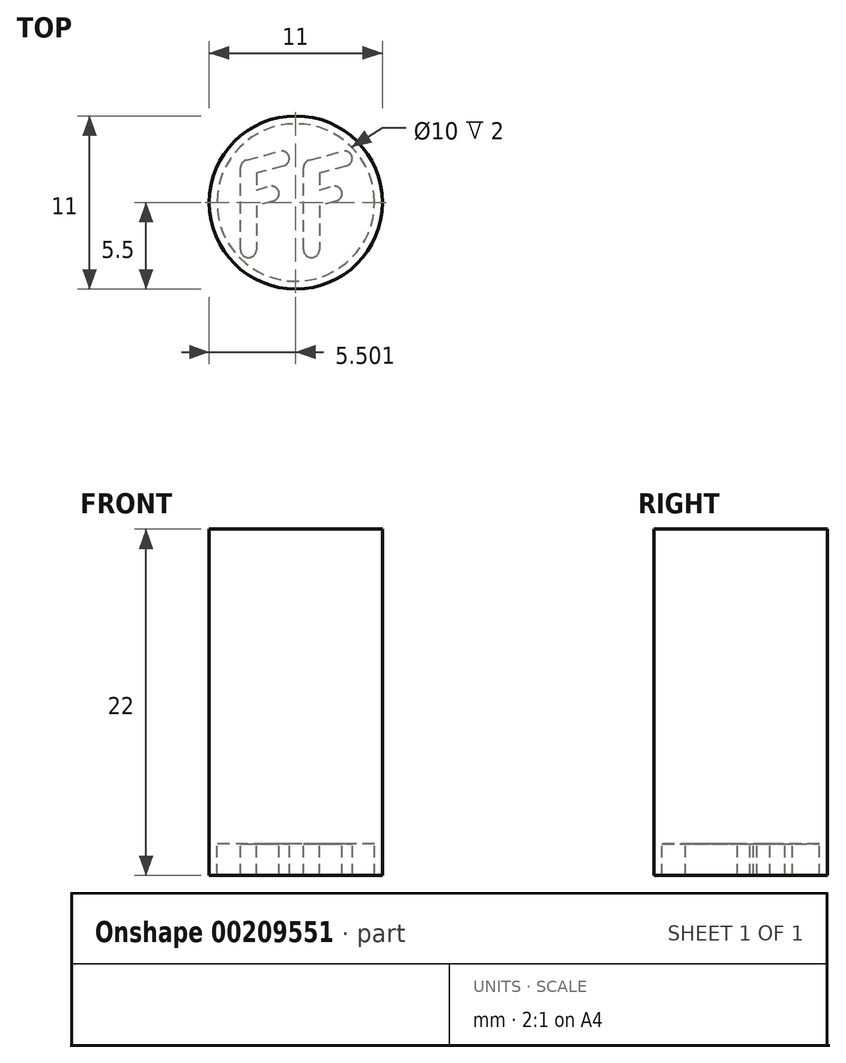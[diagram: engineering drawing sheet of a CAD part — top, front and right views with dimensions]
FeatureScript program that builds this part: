
annotation { "Feature Type Name" : "Feature", "Feature Type Description" : "" }
export const myFeature = defineFeature(function(context is Context, id is Id, definition is map)
    precondition{}
    {
        {
            var Q0;
            Q0=qCreatedBy(makeId("Top.planeOp"),FACE);
            var sketch = newSketch(context, id + "F0", { "sketchPlane" : qUnion([Q0])});
            skCircle(sketch, "E0", {"center": v(1.06, 0) * mm, "radius": 5 * mm});
            skCircle(sketch, "E1.0", {"center": v(1.06, 0) * mm, "radius": 5.5 * mm});
            skLineSegment(sketch, "E2", {"start": v(-2.44, -3.5) * mm, "end": v(-2.44, 2.6) * mm});
            skLineSegment(sketch, "E3", {"start": v(-2.44, 2.6) * mm, "end": v(0.65, 3.43) * mm});
            skLineSegment(sketch, "E4", {"start": v(0.65, 3.43) * mm, "end": v(0.65, 2.43) * mm});
            skLineSegment(sketch, "E5", {"start": v(0.65, 2.43) * mm, "end": v(-1.44, 1.87) * mm});
            skLineSegment(sketch, "E6", {"start": v(-1.44, 1.87) * mm, "end": v(-1.44, 0.8) * mm});
            skLineSegment(sketch, "E7", {"start": v(-1.44, 0.8) * mm, "end": v(0, 1.2) * mm});
            skLineSegment(sketch, "E8", {"start": v(0, 1.2) * mm, "end": v(0, 0.2) * mm});
            skLineSegment(sketch, "E9", {"start": v(0, 0.2) * mm, "end": v(-1.44, -0.2) * mm});
            skLineSegment(sketch, "E10", {"start": v(-1.44, -0.2) * mm, "end": v(-1.44, -3.5) * mm});
            skLineSegment(sketch, "E11", {"start": v(-1.44, -3.5) * mm, "end": v(-2.44, -3.5) * mm});
            skLineSegment(sketch, "E12.1.0.0", {"start": v(1.56, 2.6) * mm, "end": v(4.65, 3.43) * mm});
            skLineSegment(sketch, "E12.1.0.1", {"start": v(1.56, -3.5) * mm, "end": v(1.56, 2.6) * mm});
            skLineSegment(sketch, "E12.1.0.2", {"start": v(2.56, -3.5) * mm, "end": v(1.56, -3.5) * mm});
            skLineSegment(sketch, "E12.1.0.3", {"start": v(2.56, -0.2) * mm, "end": v(2.56, -3.5) * mm});
            skLineSegment(sketch, "E12.1.0.4", {"start": v(4, 0.2) * mm, "end": v(2.56, -0.2) * mm});
            skLineSegment(sketch, "E12.1.0.5", {"start": v(4, 1.2) * mm, "end": v(4, 0.2) * mm});
            skLineSegment(sketch, "E12.1.0.6", {"start": v(2.56, 0.8) * mm, "end": v(4, 1.2) * mm});
            skLineSegment(sketch, "E12.1.0.7", {"start": v(2.56, 1.87) * mm, "end": v(2.56, 0.8) * mm});
            skLineSegment(sketch, "E12.1.0.8", {"start": v(4.65, 2.43) * mm, "end": v(2.56, 1.87) * mm});
            skLineSegment(sketch, "E12.1.0.9", {"start": v(4.65, 3.43) * mm, "end": v(4.65, 2.43) * mm});
            skLineSegment(sketch, "E12.direction1", {"start": v(-2.44, -3.5) * mm, "end": v(1.56, -3.5) * mm, "construction": true});
            skSolve(sketch);
        }
        {
            var Q0;
            Q0=makeQuery(id+"F0.imprint","IMPRINT",FACE,{"disambiguationData":[TD([[makeQuery(id+"F0.imprint","IMPRINT",EDGE,{"derivedFrom":sQuery(id+"F0.wireOp",EDGE,"zHQ9hIKx-PDYS-FBsq-o5ZK-fU353ijLgQig")}),1.0]])]});
            var Q1;
            Q1=makeQuery(id+"F0.imprint","IMPRINT",FACE,{"disambiguationData":[TD([[makeQuery(id+"F0.imprint","IMPRINT",EDGE,{"derivedFrom":sQuery(id+"F0.wireOp",EDGE,"E0")}),-1.0]])]});
            var Q2;
            Q2=makeQuery(id+"F0.imprint","IMPRINT",FACE,{"disambiguationData":[TD([[makeQuery(id+"F0.imprint","IMPRINT",EDGE,{"derivedFrom":sQuery(id+"F0.wireOp",EDGE,"b1228f91-68a9-4bcc-a893-e14479d415e6")}),-1.0]])]});
            var Q3;
            Q3=makeQuery(id+"F0.imprint","IMPRINT",FACE,{"disambiguationData":[TD([[makeQuery(id+"F0.imprint","IMPRINT",EDGE,{"derivedFrom":sQuery(id+"F0.wireOp",EDGE,"zHQ9hIKx-PDYS-FBsq-o5ZK-fU353ijLgQig")}),-1.0]])]});
            var Q4;
            Q4=makeQuery(id+"F0.imprint","IMPRINT",FACE,{"disambiguationData":[TD([[makeQuery(id+"F0.imprint","IMPRINT",EDGE,{"derivedFrom":sQuery(id+"F0.wireOp",EDGE,"E0")}),1.0]])]});
            var Q5;
            Q5=makeQuery(id+"F0.imprint","IMPRINT",FACE,{"disambiguationData":[TD([[makeQuery(id+"F0.imprint","IMPRINT",EDGE,{"derivedFrom":sQuery(id+"F0.wireOp",EDGE,"E12.1.0.0")}),-1.0]])]});
            var Q6;
            Q6=makeQuery(id+"F0.imprint","IMPRINT",FACE,{"disambiguationData":[TD([[makeQuery(id+"F0.imprint","IMPRINT",EDGE,{"derivedFrom":sQuery(id+"F0.wireOp",EDGE,"E2")}),-1.0]])]});
            extrude(context, id + "F1", {"entities" : qUnion([Q0, Q1, Q2, Q3, Q4, Q5, Q6]), "depth" : 20 * mm});
        }
        {
            var Q0;
            Q0=makeQuery(id+"F0.imprint","IMPRINT",FACE,{"disambiguationData":[TD([[makeQuery(id+"F0.imprint","IMPRINT",EDGE,{"derivedFrom":sQuery(id+"F0.wireOp",EDGE,"zHQ9hIKx-PDYS-FBsq-o5ZK-fU353ijLgQig")}),-1.0]])]});
            var Q1;
            Q1=makeQuery(id+"F0.imprint","IMPRINT",FACE,{"disambiguationData":[TD([[makeQuery(id+"F0.imprint","IMPRINT",EDGE,{"derivedFrom":sQuery(id+"F0.wireOp",EDGE,"b1228f91-68a9-4bcc-a893-e14479d415e6")}),-1.0]])]});
            var Q2;
            Q2=makeQuery(id+"F0.imprint","IMPRINT",FACE,{"disambiguationData":[TD([[makeQuery(id+"F0.imprint","IMPRINT",EDGE,{"derivedFrom":sQuery(id+"F0.wireOp",EDGE,"E0")}),-1.0]])]});
            var Q3;
            Q3=makeQuery(id+"F0.imprint","IMPRINT",FACE,{"disambiguationData":[TD([[makeQuery(id+"F0.imprint","IMPRINT",EDGE,{"derivedFrom":sQuery(id+"F0.wireOp",EDGE,"E2")}),-1.0]])]});
            var Q4;
            Q4=makeQuery(id+"F0.imprint","IMPRINT",FACE,{"disambiguationData":[TD([[makeQuery(id+"F0.imprint","IMPRINT",EDGE,{"derivedFrom":sQuery(id+"F0.wireOp",EDGE,"E12.1.0.0")}),-1.0]])]});
            extrude(context, id + "F2", {"entities" : qUnion([Q0, Q1, Q2, Q3, Q4]), "operationType" : NewBodyOperationType.ADD, "oppositeDirection" : true, "depth" : 2 * mm});
        }
        {
            var Q0;
            Q0=makeQuery(id+"F2.opExtrude","SWEPT_EDGE",EDGE,{"disambiguationData":[OSD([sQuery(id+"F0.wireOp",EDGE,"E12.1.0.2"),sQuery(id+"F0.wireOp",EDGE,"E12.1.0.3")])]});
            var Q1;
            Q1=makeQuery(id+"F2.opExtrude","SWEPT_EDGE",EDGE,{"disambiguationData":[OSD([sQuery(id+"F0.wireOp",EDGE,"E10"),sQuery(id+"F0.wireOp",EDGE,"E11")])]});
            var Q2;
            Q2=makeQuery(id+"F2.opExtrude","SWEPT_EDGE",EDGE,{"disambiguationData":[OSD([sQuery(id+"F0.wireOp",EDGE,"E12.1.0.4"),sQuery(id+"F0.wireOp",EDGE,"E12.1.0.5")])]});
            var Q3;
            Q3=makeQuery(id+"F2.opExtrude","SWEPT_EDGE",EDGE,{"disambiguationData":[OSD([sQuery(id+"F0.wireOp",EDGE,"E8"),sQuery(id+"F0.wireOp",EDGE,"E9")])]});
            var Q4;
            Q4=makeQuery(id+"F2.opExtrude","SWEPT_EDGE",EDGE,{"disambiguationData":[OSD([sQuery(id+"F0.wireOp",EDGE,"E12.1.0.8"),sQuery(id+"F0.wireOp",EDGE,"E12.1.0.9")])]});
            var Q5;
            Q5=makeQuery(id+"F2.opExtrude","SWEPT_EDGE",EDGE,{"disambiguationData":[OSD([sQuery(id+"F0.wireOp",EDGE,"E4"),sQuery(id+"F0.wireOp",EDGE,"E5")])]});
            fillet(context, id + "F3", {"entities" : qUnion([Q0, Q1, Q2, Q3, Q4, Q5]), "radius" : 0.5 * mm, "tangentPropagation" : true, "allowEdgeOverflow" : false});
        }
        {
            var Q0;
            Q0=makeQuery(id+"F2.opExtrude","SWEPT_EDGE",EDGE,{"disambiguationData":[OSD([sQuery(id+"F0.wireOp",EDGE,"E12.1.0.0"),sQuery(id+"F0.wireOp",EDGE,"E12.1.0.9")])]});
            var Q1;
            Q1=makeQuery(id+"F2.opExtrude","SWEPT_EDGE",EDGE,{"disambiguationData":[OSD([sQuery(id+"F0.wireOp",EDGE,"E3"),sQuery(id+"F0.wireOp",EDGE,"E4")])]});
            var Q2;
            Q2=makeQuery(id+"F2.opExtrude","SWEPT_EDGE",EDGE,{"disambiguationData":[OSD([sQuery(id+"F0.wireOp",EDGE,"E7"),sQuery(id+"F0.wireOp",EDGE,"E8")])]});
            var Q3;
            Q3=makeQuery(id+"F2.opExtrude","SWEPT_EDGE",EDGE,{"disambiguationData":[OSD([sQuery(id+"F0.wireOp",EDGE,"E12.1.0.5"),sQuery(id+"F0.wireOp",EDGE,"E12.1.0.6")])]});
            var Q4;
            Q4=makeQuery(id+"F2.opExtrude","SWEPT_EDGE",EDGE,{"disambiguationData":[OSD([sQuery(id+"F0.wireOp",EDGE,"E12.1.0.1"),sQuery(id+"F0.wireOp",EDGE,"E12.1.0.2")])]});
            var Q5;
            Q5=makeQuery(id+"F2.opExtrude","SWEPT_EDGE",EDGE,{"disambiguationData":[OSD([sQuery(id+"F0.wireOp",EDGE,"E2"),sQuery(id+"F0.wireOp",EDGE,"E11")])]});
            var Q6;
            Q6=makeQuery(id+"F2.opExtrude","SWEPT_EDGE",EDGE,{"disambiguationData":[OSD([sQuery(id+"F0.wireOp",EDGE,"E12.1.0.0"),sQuery(id+"F0.wireOp",EDGE,"E12.1.0.1")])]});
            var Q7;
            Q7=makeQuery(id+"F2.opExtrude","SWEPT_EDGE",EDGE,{"disambiguationData":[OSD([sQuery(id+"F0.wireOp",EDGE,"E2"),sQuery(id+"F0.wireOp",EDGE,"E3")])]});
            fillet(context, id + "F4", {"entities" : qUnion([Q0, Q1, Q2, Q3, Q4, Q5, Q6, Q7]), "radius" : 0.5 * mm, "tangentPropagation" : true, "allowEdgeOverflow" : false});
        }
    });
